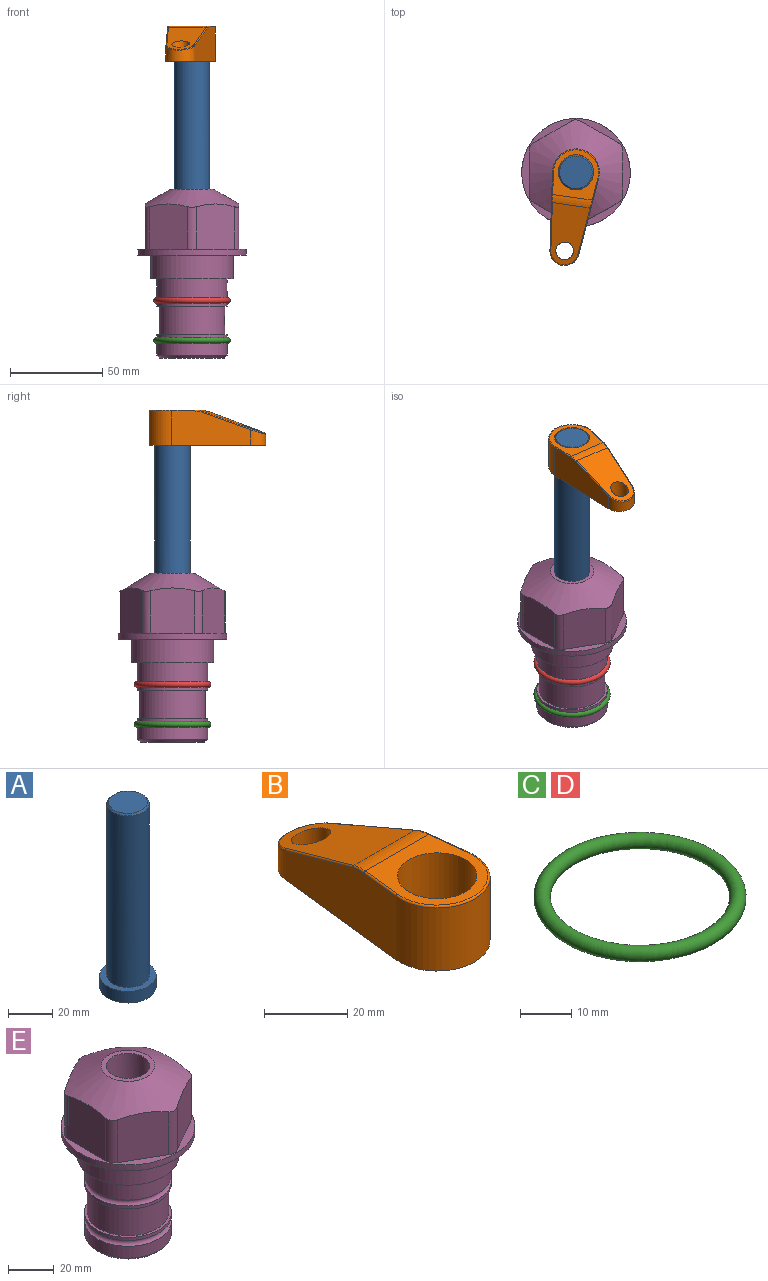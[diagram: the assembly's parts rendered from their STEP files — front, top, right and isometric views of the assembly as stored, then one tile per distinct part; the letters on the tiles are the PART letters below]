
ASSEMBLY  parts=5 mates=3
PART A: 6 faces, bbox 25.4x25.4x101.6 mm
  f0: plane 17.46x17.46mm, normal (0,0,1), area 239.5mm2, adj f5
  f1: plane 25.4x25.4mm, normal (0,0,-1), area 506.7mm2, adj f2
  f2: cylinder r=12.7mm len=25.4mm, axis (0,0,1), area 506.7mm2, adj f1,f3
  f3: plane 25.4x25.4mm, normal (0,0,1), area 221.7mm2, adj f2,f4
  f4: cylinder r=9.53mm len=94.46mm, axis (0,0,1), area 5653mm2, adj f3,f5
  f5: cone r=8.73mm half-angle=45deg, axis (0,0,-1), area 64.4mm2, adj f0,f4
PART B: 44 faces, bbox 27.5x64.5x19.1 mm
  f0: plane 2.3x0.95mm, normal (0,0,-1), area 1mm2, adj f25,f30,f34
  f1: plane 63.5x25.4mm, normal (0,0,-1), area 561.7mm2, adj f2,f3,f4,f5,f6,f7,f19,f20
  f2: cylinder r=12.7mm len=25.4mm, axis (0,0,-1), area 792.2mm2, adj f1,f3,f5,f13
  f3: plane 42.33x18.54mm, normal (0.99,0.11,0), area 647mm2, adj f1,f2,f4,f11,f12,f14
  f4: cylinder r=7.94mm len=15.78mm, axis (0,0,-1), area 158.6mm2, adj f1,f3,f5,f16
  f5: plane 42.33x18.54mm, normal (-0.99,0.11,0), area 647mm2, adj f1,f2,f4,f15,f17,f18
  f6: cylinder r=9.53mm len=19.05mm, axis (0,0,-1), area 1140.1mm2, adj f1,f8
  f7: cylinder r=4.76mm len=10.98mm, axis (0,0,-1), area 276.1mm2, adj f1,f9
  f8: plane 25.83x24.38mm, normal (0,0,1), area 262.2mm2, adj f6,f10,f11,f13,f15
  f9: plane 32.49x20.55mm, normal (0,0.34,0.94), area 489.9mm2, adj f7,f10,f14,f16,f18
  f10: cylinder r=12.7mm len=21.49mm, axis (-1,0,0), area 93.2mm2, adj f8,f9,f12,f17
  f11: cylinder r=0.51mm len=12.34mm, axis (0.11,-0.99,0), area 9.9mm2, adj f3,f8,f12,f13
  f12: bspline ~7.62x1.64mm, area 3.5mm2, adj f3,f10,f11,f14
  f13: torus R=12.19mm, axis (0,0,1), area 33.6mm2, adj f2,f8,f11,f15
  f14: cylinder r=0.51mm len=26.01mm, axis (0.1,-0.93,0.34), area 21.6mm2, adj f3,f9,f12,f16
  f15: cylinder r=0.51mm len=12.34mm, axis (0.11,0.99,0), area 9.9mm2, adj f5,f8,f13,f17
  f16: bspline ~15.78x7.05mm, area 15.7mm2, adj f4,f9,f14,f18
  f17: bspline ~7.62x1.64mm, area 3.5mm2, adj f5,f10,f15,f18
  f18: cylinder r=0.51mm len=26.01mm, axis (0.1,0.93,-0.34), area 21.6mm2, adj f5,f9,f16,f17
  f19: plane 21.6x14.29mm, normal (-0.99,-0.11,0), area 242.6mm2, adj f1,f26,f28,f34,f36,f38
  f20: plane 21.6x14.29mm, normal (0.99,-0.11,0), area 242.6mm2, adj f1,f27,f29,f37,f39,f41
  f21: cylinder r=12.7mm len=14.29mm, axis (0,0,-1), area 173.2mm2, adj f1,f26,f27,f30,f31,f33
  f22: cylinder r=7.94mm len=7.63mm, axis (0,0,-1), area 53.8mm2, adj f1,f28,f29,f42
  f23: plane 2.3x0.95mm, normal (0,0,-1), area 1mm2, adj f25,f33,f37
  f24: plane 17.94x12.32mm, normal (0,-0.34,-0.94), area 191.2mm2, adj f25,f38,f41,f42
  f25: cylinder r=9.53mm len=12.93mm, axis (-1,0,0), area 37.5mm2, adj f0,f23,f24,f31,f36,f39
  f26: cylinder r=1.59mm len=14.29mm, axis (0,0,-1), area 49mm2, adj f1,f19,f21,f32
  f27: cylinder r=1.59mm len=14.29mm, axis (0,0,-1), area 49mm2, adj f1,f20,f21,f35
  f28: cylinder r=1.59mm len=7.28mm, axis (0,0,-1), area 22.1mm2, adj f1,f19,f22,f40
  f29: cylinder r=1.59mm len=7.28mm, axis (0,0,-1), area 22.1mm2, adj f1,f20,f22,f43
  f30: torus R=14.29mm, axis (0,0,1), area 5.8mm2, adj f0,f21,f31,f32
  f31: bspline ~11.06x2.73mm, area 20.8mm2, adj f21,f25,f30,f33
  f32: sphere r=1.59mm, area 5.4mm2, adj f26,f30,f34
  f33: torus R=14.29mm, axis (0,0,1), area 5.8mm2, adj f21,f23,f31,f35
  f34: cylinder r=1.59mm len=1.68mm, axis (-0.11,0.99,0), area 2.4mm2, adj f0,f19,f32,f36
  f35: sphere r=1.59mm, area 5.4mm2, adj f27,f33,f37
  f36: bspline ~5.82x2.33mm, area 7.7mm2, adj f19,f25,f34,f38
  f37: cylinder r=1.59mm len=1.68mm, axis (0.11,0.99,0), area 2.4mm2, adj f20,f23,f35,f39
  f38: cylinder r=1.59mm len=18.33mm, axis (0.1,-0.93,0.34), area 46.7mm2, adj f19,f24,f36,f40
  f39: bspline ~5.82x2.33mm, area 7.7mm2, adj f20,f25,f37,f41
  f40: sphere r=1.59mm, area 3.6mm2, adj f28,f38,f42
  f41: cylinder r=1.59mm len=18.33mm, axis (0.1,0.93,-0.34), area 46.7mm2, adj f20,f24,f39,f43
  f42: bspline ~8.31x1.84mm, area 15.3mm2, adj f22,f24,f40,f43
  f43: sphere r=1.59mm, area 3.6mm2, adj f29,f41,f42
PART C: 1 faces, bbox 44.7x44.7x3.2 mm
  f0: torus R=19.05mm, axis (0,0,1), area 1193.9mm2
PART D: same geometry as C
PART E: 36 faces, bbox 58.7x58.7x91.2 mm
  f0: cylinder r=17.78mm len=35.56mm, axis (0,0,1), area 1670.8mm2, adj f23,f24,f31
  f1: cylinder r=19.05mm len=38.1mm, axis (0,0,1), area 1191.9mm2, adj f26,f27,f30
  f2: plane 58.66x58.66mm, normal (0,0,-1), area 1150.6mm2, adj f3,f28
  f3: cylinder r=29.33mm len=58.66mm, axis (0,0,-1), area 585.1mm2, adj f2,f4
  f4: plane 58.66x58.66mm, normal (0,0,1), area 475.9mm2, adj f3,f5,f6,f7,f8,f9,f10,f11
  f5: plane 24.5x20.32mm, normal (-0.5,0.87,0), area 562.8mm2, adj f4,f15,f16,f17
  f6: plane 24.5x20.32mm, normal (0.5,0.87,0), area 562.8mm2, adj f4,f14,f15,f17
  f7: plane 24.5x23.48mm, normal (1,0,0), area 562.8mm2, adj f4,f13,f14,f17
  f8: plane 24.5x20.32mm, normal (0.5,-0.87,0), area 562.8mm2, adj f4,f12,f13,f17
  f9: plane 24.5x20.32mm, normal (-0.5,-0.87,0), area 562.8mm2, adj f4,f11,f12,f17
  f10: plane 24.5x23.48mm, normal (-1,0,0), area 562.8mm2, adj f4,f11,f16,f17
  f11: cylinder r=5.08mm len=23.01mm, axis (0,0,-1), area 121.2mm2, adj f4,f9,f10,f17
  f12: cylinder r=5.08mm len=23.01mm, axis (0,0,-1), area 121.2mm2, adj f4,f8,f9,f17
  f13: cylinder r=5.08mm len=23.01mm, axis (0,0,-1), area 121.2mm2, adj f4,f7,f8,f17
  f14: cylinder r=5.08mm len=23.01mm, axis (0,0,-1), area 121.2mm2, adj f4,f6,f7,f17
  f15: cylinder r=5.08mm len=23.01mm, axis (0,0,-1), area 121.2mm2, adj f4,f5,f6,f17
  f16: cylinder r=5.08mm len=23.01mm, axis (0,0,-1), area 121.2mm2, adj f4,f5,f10,f17
  f17: cone r=11.73mm half-angle=60deg, axis (0,0,-1), area 2071.8mm2, adj f5,f6,f7,f8,f9,f10,f11,f12
  f18: plane 23.46x23.46mm, normal (0,0,1), area 147.4mm2, adj f17,f35
  f19: plane 34.93x34.93mm, normal (0,0,-1), area 958mm2, adj f29
  f20: cylinder r=19.05mm len=38.1mm, axis (0,0,1), area 760.1mm2, adj f21,f29
  f21: torus R=19.05mm, axis (0,0,1), area 565.3mm2, adj f20,f22
  f22: cylinder r=19.05mm len=38.1mm, axis (0,0,1), area 190mm2, adj f21,f23
  f23: plane 38.1x38.1mm, normal (0,0,1), area 146.9mm2, adj f0,f22
  f24: plane 38.1x38.1mm, normal (0,0,-1), area 146.9mm2, adj f0,f25
  f25: cylinder r=19.05mm len=38.1mm, axis (0,0,1), area 190mm2, adj f24,f26
  f26: torus R=19.05mm, axis (0,0,1), area 565.3mm2, adj f1,f25
  f27: plane 44.45x44.45mm, normal (0,0,-1), area 411.7mm2, adj f1,f28
  f28: cylinder r=22.23mm len=44.45mm, axis (0,0,1), area 1773.5mm2, adj f2,f27
  f29: cone r=19.05mm half-angle=45deg, axis (0,0,1), area 257.5mm2, adj f19,f20
  f30: cylinder r=3.17mm len=6.75mm, axis (-1,0,0), area 128mm2, adj f1,f33
  f31: cylinder r=3.17mm len=6.35mm, axis (-1,0,0), area 102.5mm2, adj f0,f33
  f32: plane 25.4x25.4mm, normal (0,0,1), area 506.7mm2, adj f33
  f33: cylinder r=12.7mm len=66.42mm, axis (0,0,-1), area 5236.2mm2, adj f30,f31,f32,f34
  f34: cone r=9.53mm half-angle=30deg, axis (0,0,-1), area 443.4mm2, adj f33,f35
  f35: cylinder r=9.53mm len=19.05mm, axis (0,0,-1), area 849mm2, adj f18,f34
PLACE A rot(axis=(0,0,-1),98.2deg) t=(0,0,50.2)mm
PLACE B rot(axis=(0,0,1),171.8deg) t=(0,0,104.81)mm
PLACE C t=(0,0,-21.59)mm
PLACE D at identity
PLACE E at identity fixed
MATE fastened C.f0 <-> E.f0  axis (0,0,1) through (0,0,-46.1)mm
MATE cylindrical A.f2 <-> E.f0  axis (0,0,1) through (0,0,75.84)mm
MATE fastened B.f2 <-> A.f2  axis (0,0,1) through (0,0,123.86)mm
